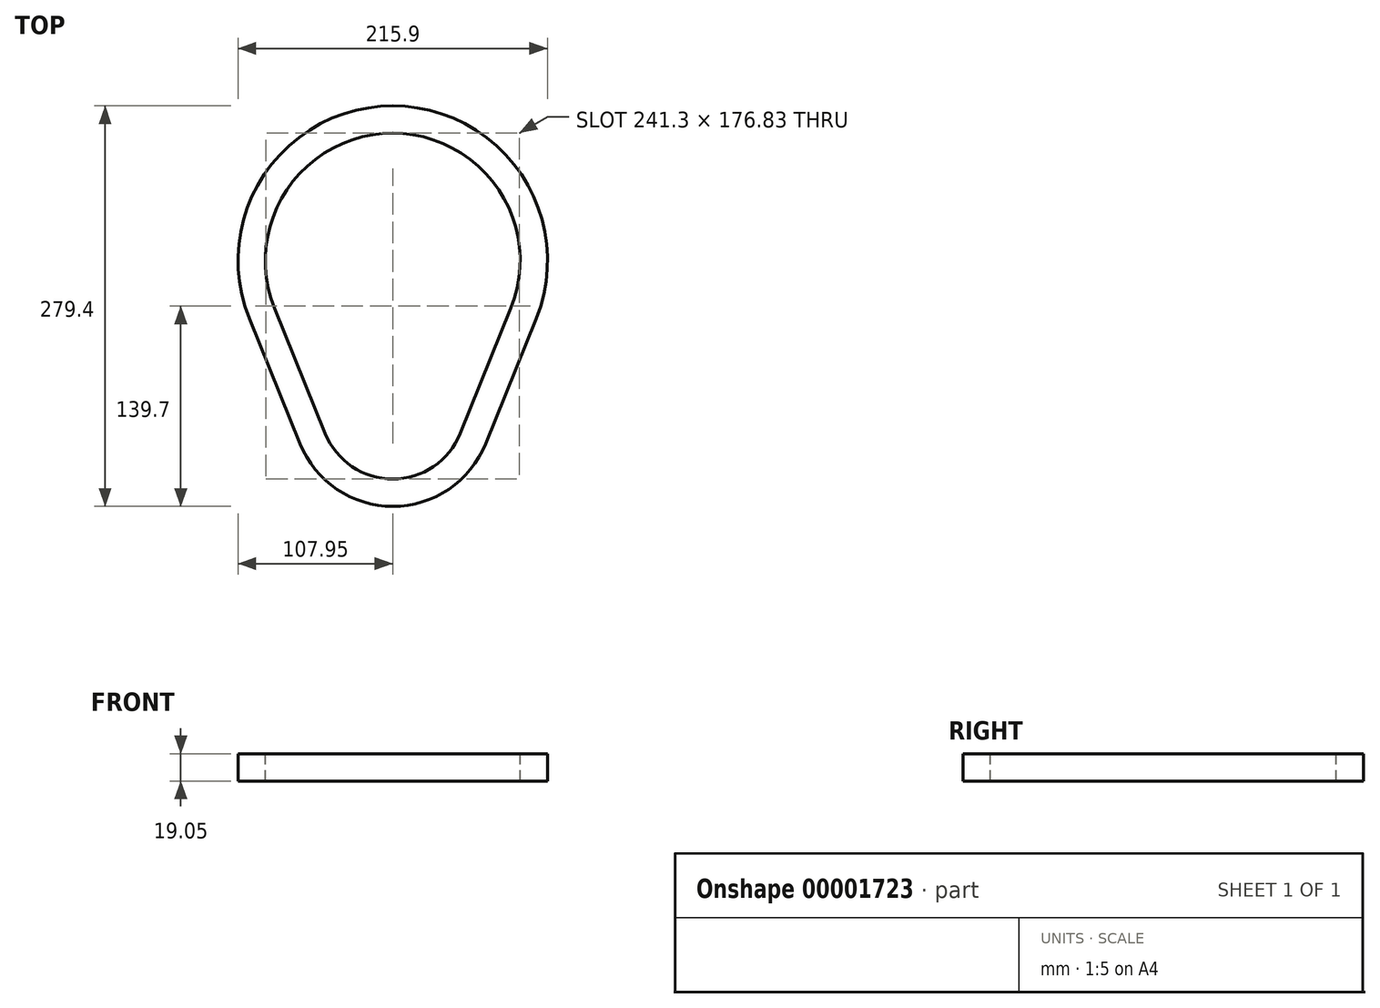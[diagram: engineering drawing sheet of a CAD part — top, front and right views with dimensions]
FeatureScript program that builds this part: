
annotation { "Feature Type Name" : "Feature", "Feature Type Description" : "" }
export const myFeature = defineFeature(function(context is Context, id is Id, definition is map)
    precondition{}
    {
        {
            var Q0;
            Q0=qCreatedBy(makeId("Top.planeOp"),FACE);
            var sketch = newSketch(context, id + "F0", { "sketchPlane" : qUnion([Q0])});
            skArc(sketch, "E0", {"start": v(82.41, 17.46) * mm, "mid": v(0, 139.7) * mm, "end": v(-82.41, 17.46) * mm});
            skArc(sketch, "E1", {"start": v(-47.1, -69.85) * mm, "mid": v(0, -101.6) * mm, "end": v(47.1, -69.85) * mm});
            skLineSegment(sketch, "E2", {"start": v(-82.41, 17.46) * mm, "end": v(-47.1, -69.85) * mm});
            skLineSegment(sketch, "E3", {"start": v(82.41, 17.46) * mm, "end": v(47.1, -69.85) * mm});
            skArc(sketch, "E4.0", {"start": v(100.07, 10.32) * mm, "mid": v(0, 158.75) * mm, "end": v(-100.07, 10.32) * mm});
            skLineSegment(sketch, "E4.1", {"start": v(100.07, 10.32) * mm, "end": v(64.75, -77) * mm});
            skArc(sketch, "E4.2", {"start": v(-64.75, -77) * mm, "mid": v(0, -120.65) * mm, "end": v(64.75, -77) * mm});
            skLineSegment(sketch, "E4.3", {"start": v(-100.07, 10.32) * mm, "end": v(-64.75, -77) * mm});
            skSolve(sketch);
        }
        {
            var Q0;
            Q0=makeQuery(id+"F0.imprint","IMPRINT",FACE,{"disambiguationData":[TD([[makeQuery(id+"F0.imprint","IMPRINT",EDGE,{"derivedFrom":sQuery(id+"F0.wireOp",EDGE,"E0")}),-1.0]])]});
            extrude(context, id + "F1", {"entities" : qUnion([Q0]), "oppositeDirection" : true, "depth" : 19.05 * mm});
        }
        {
            var Q0;
            Q0=qCreatedBy(makeId("Top.planeOp"),FACE);
            cPlane(context, id + "F2", {"entities" : qUnion([Q0]), "cplaneType" : CPlaneType.OFFSET, "offset" : 76.2 * mm, "width" : 152.4 * mm, "height" : 152.4 * mm});
        }
        {
            var Q0;
            Q0=qCreatedBy(id+"F2.planeOp",FACE);
            var sketch = newSketch(context, id + "F3", { "sketchPlane" : qUnion([Q0])});
            skCircle(sketch, "E5", {"center": v(0, 50.8) * mm, "radius": 107.95 * mm});
            skSolve(sketch);
        }
        {
            var Q0;
            Q0 = qSketchRegion(id + "F3", true);
            extrude(context, id + "F4", {"entities" : qUnion([Q0]), "depth" : 19.05 * mm});
        }
        {
            var Q0;
            Q0=qCreatedBy(makeId("Right.planeOp"),FACE);
            var sketch = newSketch(context, id + "F5", { "sketchPlane" : qUnion([Q0])});
            skLineSegment(sketch, "E6.bottom", {"start": v(156.66, 90.49) * mm, "end": v(159.83, 90.49) * mm});
            skLineSegment(sketch, "E6.top", {"start": v(156.66, 87.31) * mm, "end": v(159.83, 87.31) * mm});
            skLineSegment(sketch, "E6.left", {"start": v(156.66, 90.49) * mm, "end": v(156.66, 87.31) * mm});
            skLineSegment(sketch, "E6.right", {"start": v(159.83, 90.49) * mm, "end": v(159.83, 87.31) * mm});
            skSolve(sketch);
        }
        {
            var Q0;
            Q0 = qSketchRegion(id + "F5", true);
            var Q1;
            Q1=makeQuery(id+"F4.opExtrude","CAP_EDGE",EDGE,{"disambiguationData":[OSD([sQuery(id+"F3.wireOp",EDGE,"E5")])],"isStart":false});
            sweep(context, id + "F6", {"operationType" : NewBodyOperationType.REMOVE, "profiles" : qUnion([Q0]), "path" : qUnion([Q1])});
        }
        {
            var Q0;
            Q0=makeQuery(id+"F4.opExtrude","SWEPT_BODY",BODY,{"disambiguationData":[OSD([sQuery(id+"F3.wireOp",EDGE,"E5")])]});
            deleteBodies(context, id + "F7", {"entities" : qUnion([Q0])});
        }
    });
